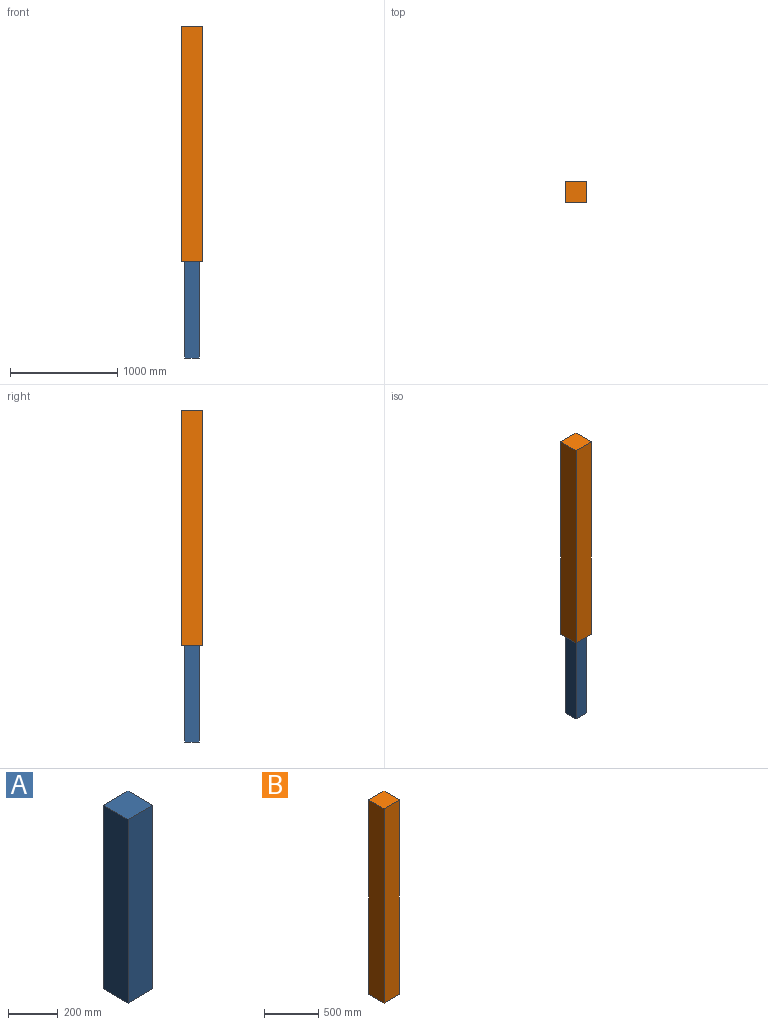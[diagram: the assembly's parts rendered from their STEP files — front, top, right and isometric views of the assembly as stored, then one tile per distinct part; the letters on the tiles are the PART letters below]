
ASSEMBLY  parts=2 mates=1
PART A: 6 faces, bbox 140x140x900 mm
  f0: plane 900x140mm, normal (0,-1,0), area 126000mm2, adj f1,f3,f4,f5
  f1: plane 900x140mm, normal (1,0,0), area 126000mm2, adj f0,f2,f4,f5
  f2: plane 900x140mm, normal (0,1,0), area 126000mm2, adj f1,f3,f4,f5
  f3: plane 900x140mm, normal (-1,0,0), area 126000mm2, adj f0,f2,f4,f5
  f4: plane 140x140mm, normal (0,0,1), area 19600mm2, adj f0,f1,f2,f3
  f5: plane 140x140mm, normal (0,0,-1), area 19600mm2, adj f0,f1,f2,f3
PART B: 6 faces, bbox 200x200x2200 mm
  f0: plane 2200x200mm, normal (0,-1,0), area 440000mm2, adj f1,f3,f4,f5
  f1: plane 2200x200mm, normal (1,0,0), area 440000mm2, adj f0,f2,f4,f5
  f2: plane 2200x200mm, normal (0,1,0), area 440000mm2, adj f1,f3,f4,f5
  f3: plane 2200x200mm, normal (-1,0,0), area 440000mm2, adj f0,f2,f4,f5
  f4: plane 200x200mm, normal (0,0,1), area 40000mm2, adj f0,f1,f2,f3
  f5: plane 200x200mm, normal (0,0,-1), area 40000mm2, adj f0,f1,f2,f3
PLACE A at identity
PLACE B at identity
MATE fastened A.f4 <-> B.f5  axis (0,0,1) through (0,0,900)mm
